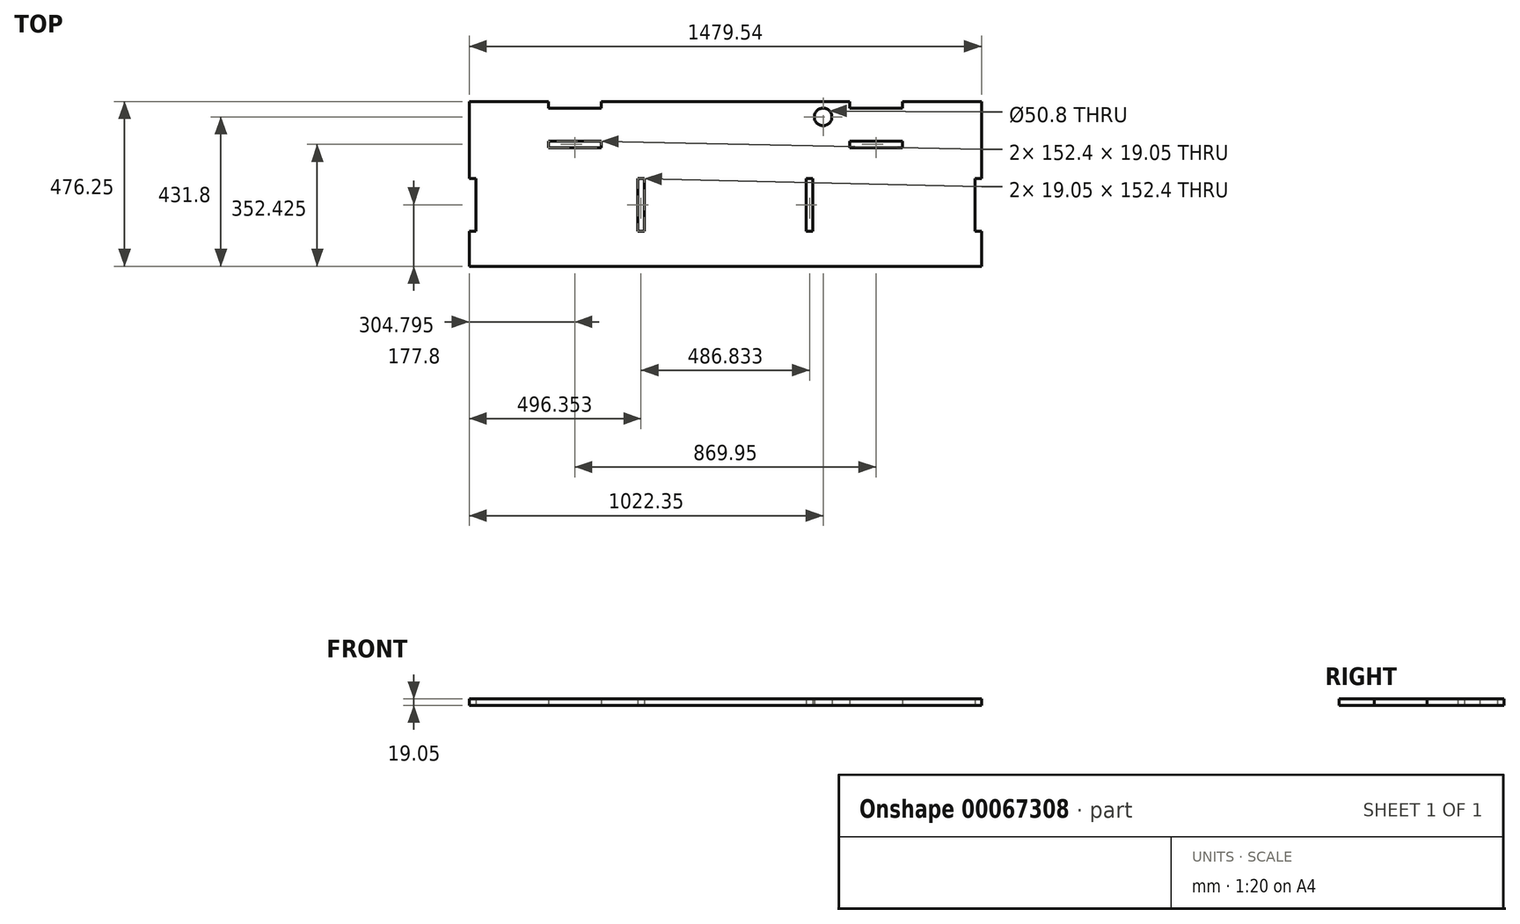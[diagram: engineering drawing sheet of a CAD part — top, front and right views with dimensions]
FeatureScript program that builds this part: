
annotation { "Feature Type Name" : "Feature", "Feature Type Description" : "" }
export const myFeature = defineFeature(function(context is Context, id is Id, definition is map)
    precondition{}
    {
        {
            var Q0;
            Q0=qCreatedBy(makeId("Top.planeOp"),FACE);
            var sketch = newSketch(context, id + "F0", { "sketchPlane" : qUnion([Q0])});
            skLineSegment(sketch, "E0.bottom", {"start": v(-739.78, 0) * mm, "end": v(739.78, 0) * mm});
            skLineSegment(sketch, "E0.top", {"start": v(-739.77, -476.25) * mm, "end": v(739.77, -476.25) * mm});
            skLineSegment(sketch, "E0.left", {"start": v(-739.78, 0) * mm, "end": v(-739.78, -476.25) * mm});
            skLineSegment(sketch, "E0.right", {"start": v(739.78, 0) * mm, "end": v(739.77, -476.25) * mm});
            skLineSegment(sketch, "E1", {"start": v(739.78, 0) * mm, "end": v(739.78, -95.25) * mm});
            skLineSegment(sketch, "E2", {"start": v(282.58, -44.45) * mm, "end": v(307.98, -44.45) * mm});
            skCircle(sketch, "E3", {"center": v(282.58, -44.45) * mm, "radius": 25.4 * mm});
            skLineSegment(sketch, "E4.bottom", {"start": v(-739.78, -222.25) * mm, "end": v(-720.73, -222.25) * mm});
            skLineSegment(sketch, "E4.top", {"start": v(-739.78, -374.65) * mm, "end": v(-720.73, -374.65) * mm});
            skLineSegment(sketch, "E4.left", {"start": v(-739.78, -222.25) * mm, "end": v(-739.78, -374.65) * mm});
            skLineSegment(sketch, "E4.right", {"start": v(-720.73, -222.25) * mm, "end": v(-720.73, -374.65) * mm});
            skLineSegment(sketch, "E5.bottom", {"start": v(739.78, -222.25) * mm, "end": v(720.73, -222.25) * mm});
            skLineSegment(sketch, "E5.top", {"start": v(739.78, -374.65) * mm, "end": v(720.73, -374.65) * mm});
            skLineSegment(sketch, "E5.left", {"start": v(739.78, -222.25) * mm, "end": v(739.78, -374.65) * mm});
            skLineSegment(sketch, "E5.right", {"start": v(720.73, -222.25) * mm, "end": v(720.73, -374.65) * mm});
            skLineSegment(sketch, "E6.bottom", {"start": v(-511.18, 0) * mm, "end": v(-358.78, 0) * mm});
            skLineSegment(sketch, "E6.top", {"start": v(-511.18, -19.05) * mm, "end": v(-358.78, -19.05) * mm});
            skLineSegment(sketch, "E6.left", {"start": v(-511.18, 0) * mm, "end": v(-511.18, -19.05) * mm});
            skLineSegment(sketch, "E6.right", {"start": v(-358.78, 0) * mm, "end": v(-358.78, -19.05) * mm});
            skLineSegment(sketch, "E7.bottom", {"start": v(358.78, 0) * mm, "end": v(511.18, 0) * mm});
            skLineSegment(sketch, "E7.top", {"start": v(358.78, -19.05) * mm, "end": v(511.18, -19.05) * mm});
            skLineSegment(sketch, "E7.left", {"start": v(358.78, 0) * mm, "end": v(358.78, -19.05) * mm});
            skLineSegment(sketch, "E7.right", {"start": v(511.18, 0) * mm, "end": v(511.18, -19.05) * mm});
            skLineSegment(sketch, "E8.bottom", {"start": v(-511.18, -114.3) * mm, "end": v(-358.78, -114.3) * mm});
            skLineSegment(sketch, "E8.top", {"start": v(-511.18, -133.35) * mm, "end": v(-358.78, -133.35) * mm});
            skLineSegment(sketch, "E8.left", {"start": v(-511.18, -114.3) * mm, "end": v(-511.18, -133.35) * mm});
            skLineSegment(sketch, "E8.right", {"start": v(-358.78, -114.3) * mm, "end": v(-358.78, -133.35) * mm});
            skLineSegment(sketch, "E9.bottom", {"start": v(358.78, -114.3) * mm, "end": v(511.18, -114.3) * mm});
            skLineSegment(sketch, "E9.top", {"start": v(358.78, -133.35) * mm, "end": v(511.18, -133.35) * mm});
            skLineSegment(sketch, "E9.left", {"start": v(358.78, -114.3) * mm, "end": v(358.78, -133.35) * mm});
            skLineSegment(sketch, "E9.right", {"start": v(511.18, -114.3) * mm, "end": v(511.18, -133.35) * mm});
            skLineSegment(sketch, "E10.bottom", {"start": v(-252.94, -222.25) * mm, "end": v(-233.9, -222.25) * mm});
            skLineSegment(sketch, "E10.top", {"start": v(-252.94, -374.65) * mm, "end": v(-233.9, -374.65) * mm});
            skLineSegment(sketch, "E10.left", {"start": v(-252.94, -222.25) * mm, "end": v(-252.94, -374.65) * mm});
            skLineSegment(sketch, "E10.right", {"start": v(-233.9, -222.25) * mm, "end": v(-233.9, -374.65) * mm});
            skLineSegment(sketch, "E11.bottom", {"start": v(233.9, -222.25) * mm, "end": v(252.94, -222.25) * mm});
            skLineSegment(sketch, "E11.top", {"start": v(233.9, -374.65) * mm, "end": v(252.94, -374.65) * mm});
            skLineSegment(sketch, "E11.left", {"start": v(233.9, -222.25) * mm, "end": v(233.9, -374.65) * mm});
            skLineSegment(sketch, "E11.right", {"start": v(252.94, -222.25) * mm, "end": v(252.94, -374.65) * mm});
            skSolve(sketch);
        }
        {
            var Q0;
            Q0=makeQuery(id+"F0.imprint","IMPRINT",FACE,{"disambiguationData":[TD([[makeQuery(id+"F0.imprint","IMPRINT",EDGE,{"derivedFrom":sQuery(id+"F0.wireOp",EDGE,"E0.bottom")}),-1.0]])]});
            extrude(context, id + "F1", {"entities" : qUnion([Q0]), "depth" : 19.05 * mm});
        }
    });
